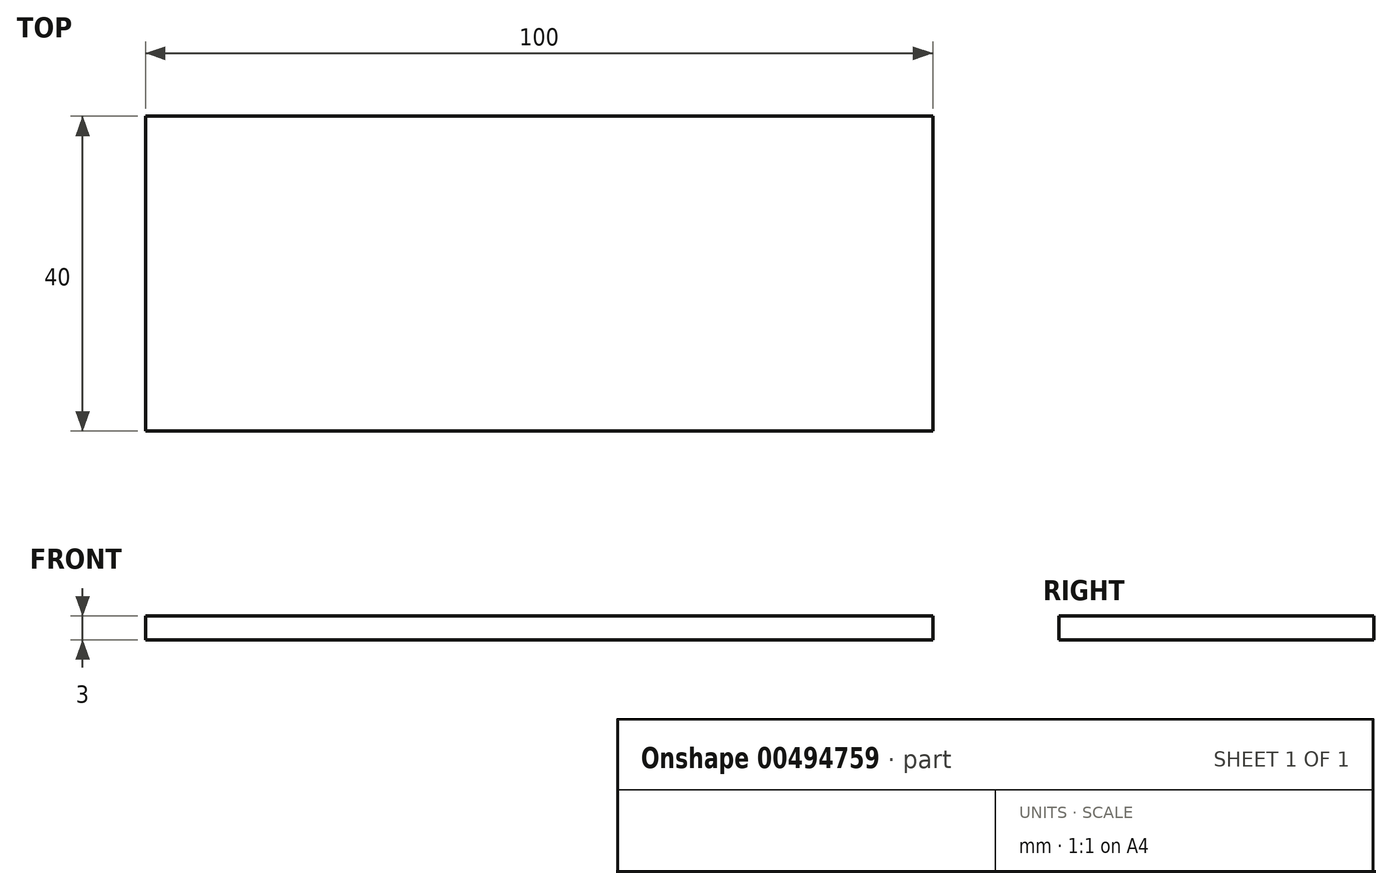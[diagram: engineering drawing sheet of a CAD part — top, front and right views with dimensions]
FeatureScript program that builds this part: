
annotation { "Feature Type Name" : "Feature", "Feature Type Description" : "" }
export const myFeature = defineFeature(function(context is Context, id is Id, definition is map)
    precondition{}
    {
        {
            var Q0;
            Q0=qCreatedBy(makeId("Top.planeOp"),FACE);
            var sketch = newSketch(context, id + "F0", { "sketchPlane" : qUnion([Q0])});
            skLineSegment(sketch, "E0.bottom", {"start": v(-43.52, 11.9) * mm, "end": v(56.48, 11.9) * mm});
            skLineSegment(sketch, "E0.top", {"start": v(-43.52, -28.1) * mm, "end": v(56.48, -28.1) * mm});
            skLineSegment(sketch, "E0.left", {"start": v(-43.52, 11.9) * mm, "end": v(-43.52, -28.1) * mm});
            skLineSegment(sketch, "E0.right", {"start": v(56.48, 11.9) * mm, "end": v(56.48, -28.1) * mm});
            skSolve(sketch);
        }
        {
            var Q0;
            Q0 = qSketchRegion(id + "F0", true);
            extrude(context, id + "F1", {"entities" : qUnion([Q0]), "depth" : 3 * mm});
        }
    });
